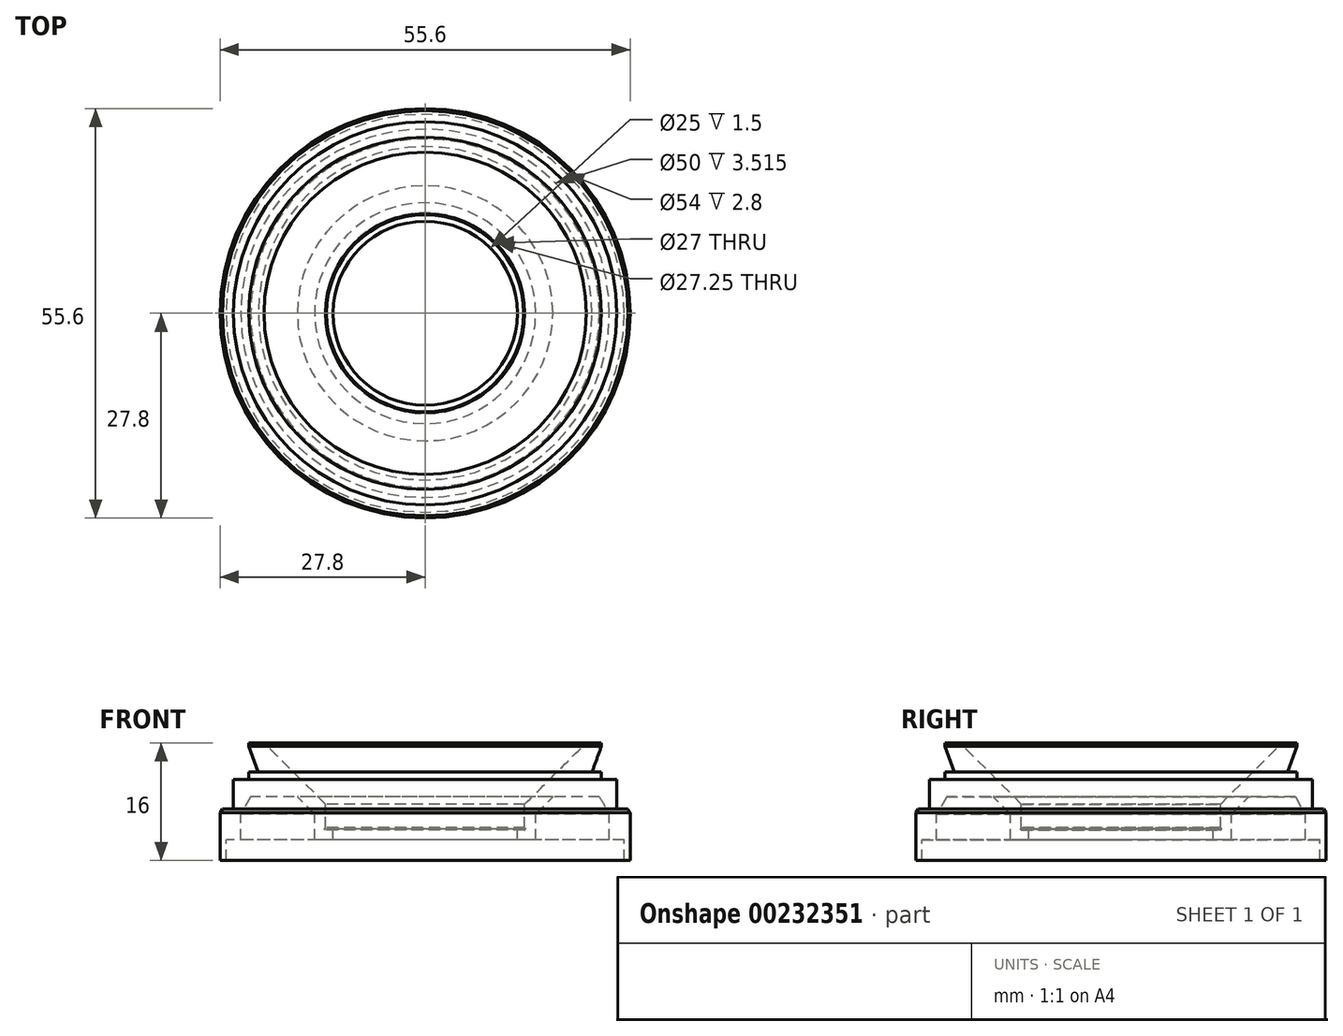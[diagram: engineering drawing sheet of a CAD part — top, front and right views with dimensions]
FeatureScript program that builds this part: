
annotation { "Feature Type Name" : "Feature", "Feature Type Description" : "" }
export const myFeature = defineFeature(function(context is Context, id is Id, definition is map)
    precondition{}
    {
        {
            var Q0;
            Q0=qCreatedBy(makeId("Front.planeOp"),FACE);
            var sketch = newSketch(context, id + "F0", { "sketchPlane" : qUnion([Q0])});
            skLineSegment(sketch, "E0", {"start": v(0, 0) * mm, "end": v(38.77, 0) * mm, "construction": true});
            skLineSegment(sketch, "E1", {"start": v(12.5, -34.5) * mm, "end": v(13.38, -34.5) * mm});
            skLineSegment(sketch, "E2", {"start": v(13.5, -34.36) * mm, "end": v(13.5, -31.16) * mm});
            skLineSegment(sketch, "E3", {"start": v(21.86, -22.8) * mm, "end": v(23.9, -22.8) * mm});
            skLineSegment(sketch, "E4", {"start": v(23.9, -27.8) * mm, "end": v(26, -27.8) * mm});
            skLineSegment(sketch, "E5", {"start": v(27.8, -38.8) * mm, "end": v(27, -38.8) * mm});
            skLineSegment(sketch, "E6", {"start": v(25, -36) * mm, "end": v(25, -32.49) * mm});
            skLineSegment(sketch, "E7", {"start": v(23.66, -30.16) * mm, "end": v(17.33, -30.16) * mm});
            skLineSegment(sketch, "E8", {"start": v(15, -32.49) * mm, "end": v(15, -36) * mm});
            skLineSegment(sketch, "E9", {"start": v(12.5, -36) * mm, "end": v(12.5, -34.5) * mm});
            skLineSegment(sketch, "E10", {"start": v(23.9, -22.8) * mm, "end": v(23.9, -23.3) * mm});
            skLineSegment(sketch, "E11", {"start": v(23.9, -23.3) * mm, "end": v(22.63, -26.8) * mm});
            skCircle(sketch, "E12.cCircle", {"center": v(13.5, -34.5) * mm, "radius": 0.12 * mm, "construction": true});
            skLineSegment(sketch, "E12.0", {"start": v(13.38, -34.57) * mm, "end": v(13.38, -34.5) * mm});
            skLineSegment(sketch, "E12.2", {"start": v(13.5, -34.36) * mm, "end": v(13.62, -34.43) * mm});
            skLineSegment(sketch, "E12.3", {"start": v(13.62, -34.43) * mm, "end": v(13.62, -34.57) * mm});
            skLineSegment(sketch, "E12.4", {"start": v(13.63, -34.57) * mm, "end": v(13.5, -34.64) * mm});
            skLineSegment(sketch, "E12.5", {"start": v(13.5, -34.64) * mm, "end": v(13.38, -34.57) * mm});
            skPoint(sketch, "E12.0.midPoint", {"position": v(13.38, -34.5) * mm});
            skPoint(sketch, "E13.orphan", {"position": v(13.38, -34.43) * mm});
            skLineSegment(sketch, "E14", {"start": v(15, -32.49) * mm, "end": v(17.33, -30.16) * mm});
            skLineSegment(sketch, "E15", {"start": v(21.86, -22.8) * mm, "end": v(13.5, -31.16) * mm});
            skLineSegment(sketch, "E16", {"start": v(22.63, -26.8) * mm, "end": v(23.9, -26.8) * mm});
            skLineSegment(sketch, "E17", {"start": v(23.9, -26.8) * mm, "end": v(23.9, -27.8) * mm});
            skLineSegment(sketch, "E18", {"start": v(26, -27.8) * mm, "end": v(26, -31.8) * mm});
            skLineSegment(sketch, "E19", {"start": v(26, -31.8) * mm, "end": v(27.5, -31.8) * mm});
            skLineSegment(sketch, "E20", {"start": v(25, -32.49) * mm, "end": v(23.66, -30.16) * mm});
            skLineSegment(sketch, "E21", {"start": v(12.5, -36) * mm, "end": v(15, -36) * mm});
            skLineSegment(sketch, "E22", {"start": v(25, -36) * mm, "end": v(27, -36) * mm});
            skLineSegment(sketch, "E23", {"start": v(27, -36) * mm, "end": v(27, -38.8) * mm});
            skLineSegment(sketch, "E24", {"start": v(27.5, -31.8) * mm, "end": v(27.8, -32.32) * mm});
            skLineSegment(sketch, "E25", {"start": v(27.8, -32.32) * mm, "end": v(27.8, -38.8) * mm});
            skSolve(sketch);
        }
        {
            var Q0;
            Q0=qCreatedBy(makeId("Front.planeOp"),FACE);
            var sketch = newSketch(context, id + "F1", { "sketchPlane" : qUnion([Q0])});
            skLineSegment(sketch, "E26", {"start": v(0, 18.59) * mm, "end": v(0, -50.05) * mm, "construction": true});
            skSolve(sketch);
        }
        {
            var Q0;
            Q0 = qSketchRegion(id + "F0", true);
            var Q1;
            Q1=sQuery(id+"F1.wireOp",EDGE,"E26");
            revolve(context, id + "F2", {"entities" : qUnion([Q0]), "axis" : qUnion([Q1]), "revolveType" : RevolveType.FULL});
        }
    });
